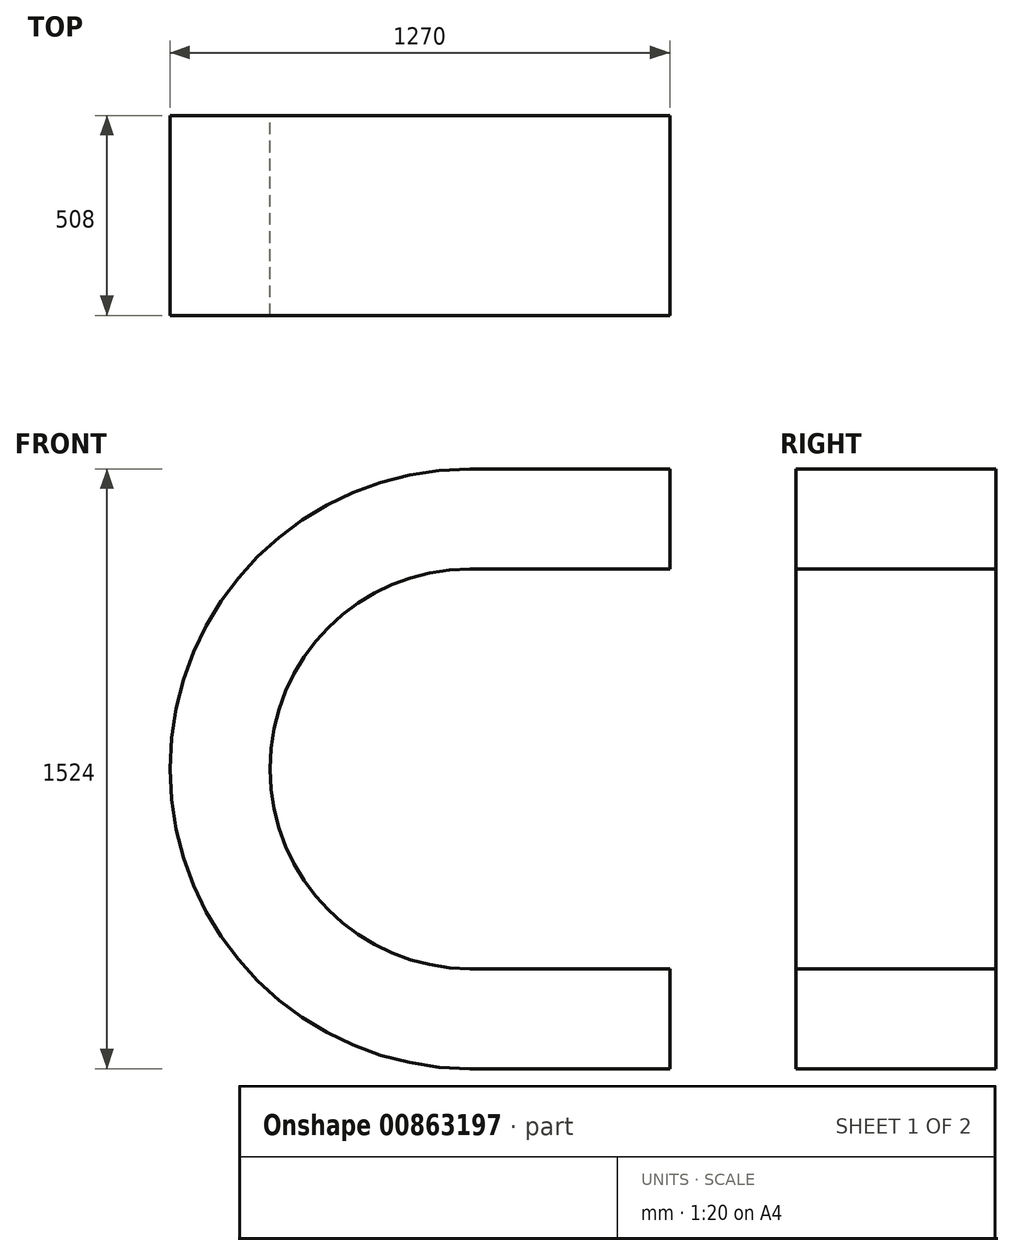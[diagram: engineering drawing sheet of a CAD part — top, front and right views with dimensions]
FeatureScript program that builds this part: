
annotation { "Feature Type Name" : "Feature", "Feature Type Description" : "" }
export const myFeature = defineFeature(function(context is Context, id is Id, definition is map)
    precondition{}
    {
        {
            var Q0;
            Q0=qCreatedBy(makeId("Front.planeOp"),FACE);
            var sketch = newSketch(context, id + "F0", { "sketchPlane" : qUnion([Q0])});
            skLineSegment(sketch, "E0", {"start": v(0, 0) * mm, "end": v(0, 1524) * mm});
            skLineSegment(sketch, "E1", {"start": v(0, 1524) * mm, "end": v(-1524, 1524) * mm});
            skLineSegment(sketch, "E2", {"start": v(0, 0) * mm, "end": v(-1524, 0) * mm});
            skLineSegment(sketch, "E3", {"start": v(-1524, 0) * mm, "end": v(-1524, 254) * mm});
            skLineSegment(sketch, "E4", {"start": v(-1524, 1524) * mm, "end": v(-1524, 1270) * mm});
            skLineSegment(sketch, "E5", {"start": v(-1524, 1270) * mm, "end": v(-2032, 1270) * mm});
            skLineSegment(sketch, "E6", {"start": v(-1524, 254) * mm, "end": v(-2032, 254) * mm});
            skArc(sketch, "E7", {"start": v(-2032, 1270) * mm, "mid": v(-2540, 762) * mm, "end": v(-2032, 254) * mm});
            skPoint(sketch, "E7.centerSnap0", {"position": v(0, 762) * mm});
            skCircle(sketch, "E8", {"center": v(-2032, 762) * mm, "radius": 254 * mm});
            skArc(sketch, "E9", {"start": v(-2032, 1524) * mm, "mid": v(-2794, 762) * mm, "end": v(-2032, 0) * mm});
            skLineSegment(sketch, "E10", {"start": v(-1524, 0) * mm, "end": v(-2032, 0) * mm});
            skLineSegment(sketch, "E11", {"start": v(-1524, 1524) * mm, "end": v(-2032, 1524) * mm});
            skLineSegment(sketch, "E12", {"start": v(0, 0) * mm, "end": v(0, 186.43) * mm});
            skSolve(sketch);
        }
        {
            var Q0;
            Q0=makeQuery(id+"F0.imprint","IMPRINT",FACE,{"disambiguationData":[TD([[makeQuery(id+"F0.imprint","IMPRINT",EDGE,{"derivedFrom":sQuery(id+"F0.wireOp",EDGE,"E3")}),1.0]])]});
            extrude(context, id + "F1", {"entities" : qUnion([Q0]), "depth" : 508 * mm, "offsetDistance" : 25.4 * mm});
        }
    });
